# Revit family: QF_GIORIK_EMG5_EMG52_ECG52_ETG5
name_source: partatom
category: Specialty Equipment
revit_build: Autodesk Revit 2014 (Build: 20140709_2115(x64)
units: mm (PartAtom-declared; Revit-internal decimal feet)

## types (4) — shared parameters
Apparent Power = 300 VA
Assembly Code = E1090320
Cold Water Connection Height = 170 mm  [stored 0.557743 ft]
Cold Water Size = 1"
Cold Water Temperature Recommended = 0 °C
Cycle = 50 Hz
FL Amps = 0 A
Gas Connection Height = 56 mm  [stored 0.183727 ft]
Gas Input = 9600 W
Gas KW = 9.6
Gas Size = 1/2"
HP = 0
Indirect Waste Connection Height = 87 mm  [stored 0.285433 ft]
Indirect Waste Flow = 0.0 L/s
Indirect Waste Size = 1 1/2"
Manufacturer = GIORIK
Max Overcurrent Protection = 16 A
Min Ckt Ampacity = 0 A
Phase = 1
URL = www.giorik.com
Volts = 230 V
Waste Water Discharge Temperature = 0 °C
Watts = 300 W
Weight in Pounds = 264.555

## per-type parameters (varying)
| type | Description | Electromechanical control | Electromechanical control with fan speed | Electromechanical control with humidifier | Touch screen control |
| EMG52 | GAS OVEN 5 GN 1/1 - 600X400 ELECTROMECHANICAL CONTROL WITH HUMIDIFIER AND TWO FAN SPEED | No | No | Yes | No |
| ECG52 | GAS OVEN 5 GN 1/1 - 600X400 ELECTROMECHANICAL CONTROL WITH TWO FAN SPEED | No | Yes | No | No |
| EMG5 | GAS OVEN 5 GN 1/1 - 600X400 ELECTROMECHANICAL CONTROL WITHOUT HUMIDIFIER | Yes | No | No | No |
| ETG5 | GAS OVEN 5 GN 1/1 - 600X400 TOUCH SCREEN CONTROL | No | No | No | Yes |

note: column(s) folded — value = type name in every type: Model

note: [stored X ft] marks values corroborated as IEEE doubles in the binary element streams (Revit-internal decimal feet)

## geometry (parser evidence)
native form markers: Blend x8, Sweep x2
no freeform markers — native parametric forms only
